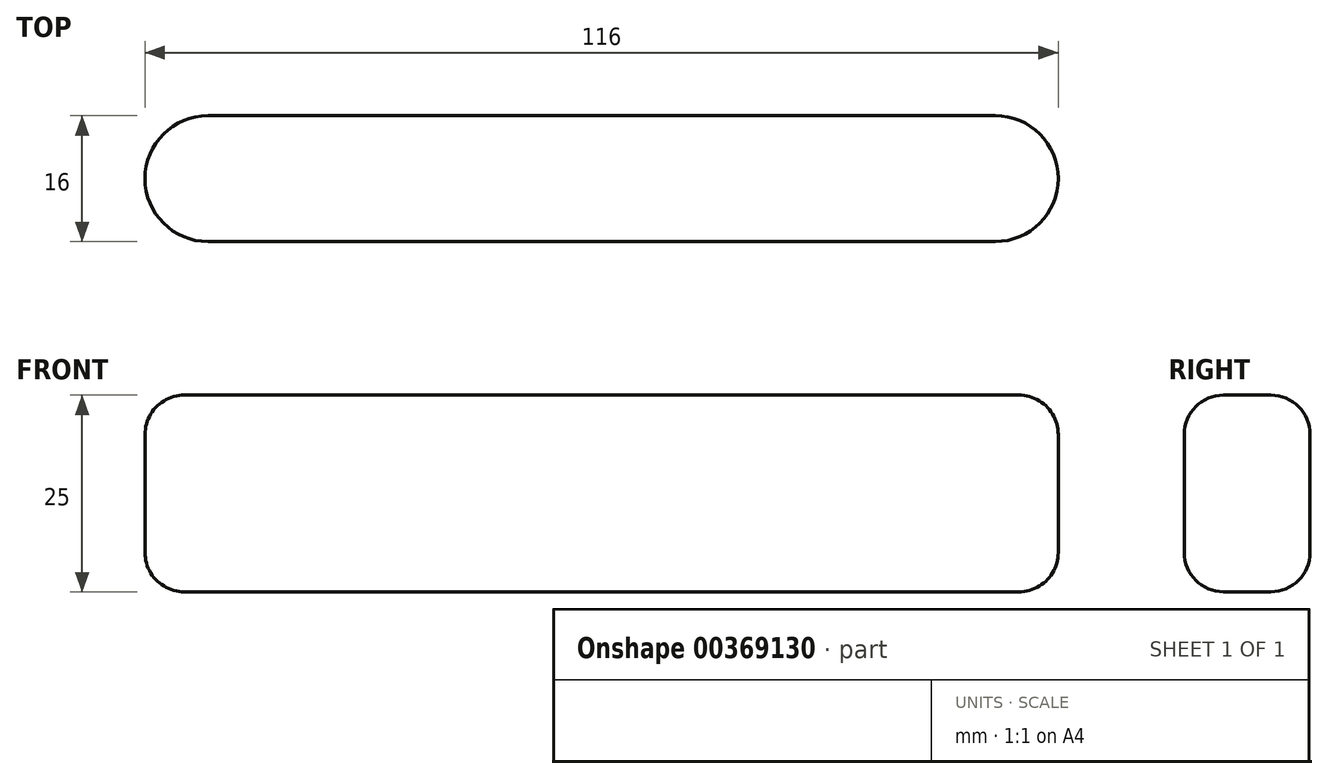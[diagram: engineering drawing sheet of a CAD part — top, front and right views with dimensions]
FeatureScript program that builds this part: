
annotation { "Feature Type Name" : "Feature", "Feature Type Description" : "" }
export const myFeature = defineFeature(function(context is Context, id is Id, definition is map)
    precondition{}
    {
        {
            var Q0;
            Q0=qCreatedBy(makeId("Top.planeOp"),FACE);
            var sketch = newSketch(context, id + "F0", { "sketchPlane" : qUnion([Q0])});
            skLineSegment(sketch, "E0.bottom", {"start": v(-50, -8) * mm, "end": v(50, -8) * mm});
            skLineSegment(sketch, "E0.top", {"start": v(-50, 8) * mm, "end": v(50, 8) * mm});
            skLineSegment(sketch, "E0.left", {"start": v(-50, -8) * mm, "end": v(-50, 8) * mm});
            skLineSegment(sketch, "E0.right", {"start": v(50, -8) * mm, "end": v(50, 8) * mm});
            skPoint(sketch, "E0.middle", {"position": v(0, 0) * mm});
            skArc(sketch, "E1", {"start": v(-50, 8) * mm, "mid": v(-58, 0) * mm, "end": v(-50, -8) * mm});
            skArc(sketch, "E2", {"start": v(50, -8) * mm, "mid": v(58, 0) * mm, "end": v(50, 8) * mm});
            skSolve(sketch);
        }
        {
            var Q0;
            Q0 = qSketchRegion(id + "F0", true);
            extrude(context, id + "F1", {"entities" : qUnion([Q0]), "depth" : 25 * mm});
        }
        {
            var Q0;
            Q0=makeQuery(id+"F1.opExtrude","CAP_EDGE",EDGE,{"disambiguationData":[OSD([sQuery(id+"F0.wireOp",EDGE,"E0.top")])],"isStart":false});
            var Q1;
            Q1=makeQuery(id+"F1.opExtrude","CAP_EDGE",EDGE,{"disambiguationData":[OSD([sQuery(id+"F0.wireOp",EDGE,"E0.bottom")])],"isStart":false});
            var Q2;
            Q2=makeQuery(id+"F1.opExtrude","CAP_EDGE",EDGE,{"disambiguationData":[OSD([sQuery(id+"F0.wireOp",EDGE,"E1")])],"isStart":false});
            var Q3;
            Q3=makeQuery(id+"F1.opExtrude","CAP_EDGE",EDGE,{"disambiguationData":[OSD([sQuery(id+"F0.wireOp",EDGE,"E2")])],"isStart":false});
            var Q4;
            Q4=makeQuery(id+"F1.opExtrude","CAP_EDGE",EDGE,{"disambiguationData":[OSD([sQuery(id+"F0.wireOp",EDGE,"E0.bottom")])],"isStart":true});
            fillet(context, id + "F2", {"entities" : qUnion([Q0, Q1, Q2, Q3, Q4]), "radius" : 5 * mm, "tangentPropagation" : true, "allowEdgeOverflow" : false});
        }
    });
